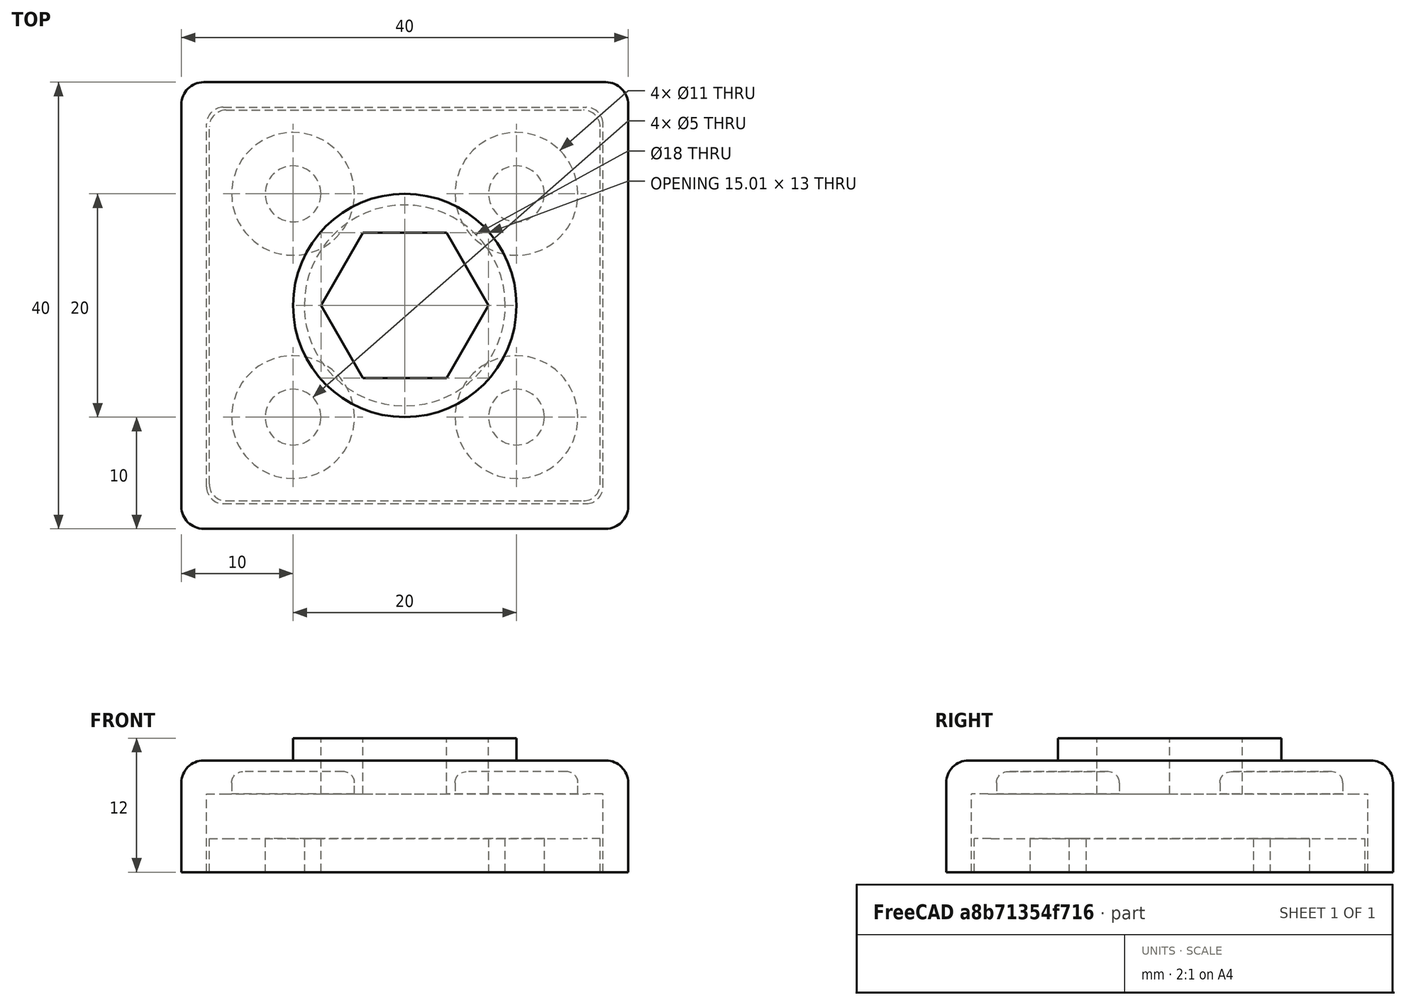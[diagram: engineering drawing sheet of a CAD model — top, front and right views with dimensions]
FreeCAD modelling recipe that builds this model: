
FCSTD DOCUMENT  (FreeCAD 1.0R39109 (Git))
Label: LowPowerConnectorCover
License: All rights reserved
LicenseURL: https://en.wikipedia.org/wiki/All_rights_reserved
objects: Part::Cut×11, Part::Cylinder×10, Part::Fillet×7, Part::Box×3, App::Part×2, Part::Prism×1, Part::MultiFuse×1
note: 33 computed .brp shape members not serialized (recipe doc carries the construction recipe); baked Part::Feature solids carry a one-line shape summary decoded from their .brp

FEATURE [Part::Box] Box  label="Cube"
  AttacherType = Attacher::AttachEngine3D
  Height = 10
  Length = 40
  Width = 40
FEATURE [Part::Cylinder] Cylinder
  Angle = 360
  AttacherType = Attacher::AttachEngine3D
  FirstAngle = 0
  Height = 12
  Placement = pos=(20,20,0) rot=(0,0,1;0rad)
  Radius = 10
  SecondAngle = 0
FEATURE [Part::Box] Box001  label="Cube001"
  AttacherType = Attacher::AttachEngine3D
  Height = 7
  Length = 35.5
  Placement = pos=(2.25,2.25,0) rot=(0,0,1;0rad)
  Width = 35.5
FEATURE [Part::Prism] Prism
  AttacherType = Attacher::AttachEngine3D
  Circumradius = 7.505
  FirstAngle = 0
  Height = 12
  Placement = pos=(20,20,0) rot=(0,0,1;0rad)
  Polygon = 6
  SecondAngle = 0
FEATURE [Part::MultiFuse] Fusion
  Shapes = -> [Box,Cylinder]
FEATURE [Part::Cut] Cut
  Base = -> Fusion
  Tool = -> Prism
FEATURE [Part::Fillet] Fillet
  Base = -> Box001
  EdgeLinks = -> Box001 [Edge1,Edge3,Edge5,Edge7]
  Edges = 4 edges r=1.5: [Edge1,Edge3,Edge5,Edge7]
FEATURE [Part::Fillet] Fillet001
  Base = -> Cut
  EdgeLinks = -> Cut [Edge1,Edge2,Edge3,Edge6,Edge7,Edge8,Edge9,Edge12]
  Edges = 8 edges r=2: [Edge1,Edge2,Edge3,Edge6,Edge7,Edge8,Edge9,Edge12]
FEATURE [Part::Cut] Cut001
  Base = -> Fillet001
  Tool = -> Fillet
FEATURE [Part::Box] Box002  label="Cube002"
  AttacherType = Attacher::AttachEngine3D
  Height = 3
  Length = 35
  Placement = pos=(2.5,2.5,0) rot=(0,0,1;0rad)
  Width = 35
FEATURE [Part::Cylinder] Cylinder001
  Angle = 360
  AttacherType = Attacher::AttachEngine3D
  FirstAngle = 0
  Height = 3
  Placement = pos=(20,20,0) rot=(0,0,1;0rad)
  Radius = 9
  SecondAngle = 0
FEATURE [Part::Cylinder] Cylinder002
  Angle = 360
  AttacherType = Attacher::AttachEngine3D
  FirstAngle = 0
  Height = 3
  Placement = pos=(10,10,0) rot=(0,0,1;0rad)
  Radius = 2.5
  SecondAngle = 0
FEATURE [Part::Cylinder] Cylinder003
  Angle = 360
  AttacherType = Attacher::AttachEngine3D
  FirstAngle = 0
  Height = 3
  Placement = pos=(30,10,0) rot=(0,0,1;0rad)
  Radius = 2.5
  SecondAngle = 0
FEATURE [Part::Cylinder] Cylinder004
  Angle = 360
  AttacherType = Attacher::AttachEngine3D
  FirstAngle = 0
  Height = 3
  Placement = pos=(10,30,0) rot=(0,0,1;0rad)
  Radius = 2.5
  SecondAngle = 0
FEATURE [Part::Cylinder] Cylinder005
  Angle = 360
  AttacherType = Attacher::AttachEngine3D
  FirstAngle = 0
  Height = 3
  Placement = pos=(30,30,0) rot=(0,0,1;0rad)
  Radius = 2.5
  SecondAngle = 0
FEATURE [Part::Fillet] Fillet002
  Base = -> Box002
  EdgeLinks = -> Box002 [Edge1,Edge3,Edge5,Edge7]
  Edges = 4 edges r=1.5: [Edge1,Edge3,Edge5,Edge7]
FEATURE [Part::Cut] Cut002
  Base = -> Fillet002
  Tool = -> Cylinder005
FEATURE [Part::Cut] Cut003
  Base = -> Cut002
  Tool = -> Cylinder004
FEATURE [Part::Cut] Cut004
  Base = -> Cut003
  Tool = -> Cylinder003
FEATURE [Part::Cut] Cut005
  Base = -> Cut004
  Tool = -> Cylinder001
FEATURE [Part::Cut] Cut006
  Base = -> Cut005
  Tool = -> Cylinder002
FEATURE [App::Part] Part001  label="Pad"
  Group = -> [Cut002,Cylinder004,Cut004,Cut003,Cut005,Cylinder002,Cylinder001,Box002,Cylinder005,Cylinder003,Fillet002,Cut006]
  Origin = -> Origin001
FEATURE [Part::Cylinder] Cylinder006
  Angle = 360
  AttacherType = Attacher::AttachEngine3D
  FirstAngle = 0
  Height = 2
  Radius = 5.5
  SecondAngle = 0
FEATURE [Part::Fillet] Fillet003
  Base = -> Cylinder006
  EdgeLinks = -> Cylinder006 [Edge3]
  Edges = 1 edges r=1: [Edge3]
  Placement = pos=(10,10,7) rot=(0,0,1;0rad)
FEATURE [Part::Cylinder] Cylinder007
  Angle = 360
  AttacherType = Attacher::AttachEngine3D
  FirstAngle = 0
  Height = 2
  Radius = 5.5
  SecondAngle = 0
FEATURE [Part::Fillet] Fillet004
  Base = -> Cylinder007
  EdgeLinks = -> Cylinder007 [Edge3]
  Edges = 1 edges r=1: [Edge3]
  Placement = pos=(30,10,7) rot=(0,0,1;0rad)
FEATURE [Part::Cylinder] Cylinder008
  Angle = 360
  AttacherType = Attacher::AttachEngine3D
  FirstAngle = 0
  Height = 2
  Radius = 5.5
  SecondAngle = 0
FEATURE [Part::Fillet] Fillet005
  Base = -> Cylinder008
  EdgeLinks = -> Cylinder008 [Edge3]
  Edges = 1 edges r=1: [Edge3]
  Placement = pos=(10,30,7) rot=(0,0,1;0rad)
FEATURE [Part::Cylinder] Cylinder009
  Angle = 360
  AttacherType = Attacher::AttachEngine3D
  FirstAngle = 0
  Height = 2
  Radius = 5.5
  SecondAngle = 0
FEATURE [Part::Fillet] Fillet006
  Base = -> Cylinder009
  EdgeLinks = -> Cylinder009 [Edge3]
  Edges = 1 edges r=1: [Edge3]
  Placement = pos=(30,30,7) rot=(0,0,1;0rad)
FEATURE [Part::Cut] Cut007
  Base = -> Cut001
  Tool = -> Fillet004
FEATURE [Part::Cut] Cut008
  Base = -> Cut007
  Tool = -> Fillet003
FEATURE [Part::Cut] Cut009
  Base = -> Cut008
  Tool = -> Fillet006
FEATURE [Part::Cut] Cut010
  Base = -> Cut009
  Tool = -> Fillet005
FEATURE [App::Part] Part  label="Cover"
  Group = -> [Fillet003,Fusion,Cut,Cut001,Cut009,Cylinder009,Cylinder008,Fillet006,Cylinder006,Cut008,Cut007,Fillet,Fillet005,Cylinder007,Fillet004,Cylinder,Box001,Box,Prism,Fillet001,Cut010]
  Origin = -> Origin
  Placement = pos=(0,0,10) rot=(0,0,1;0rad)
